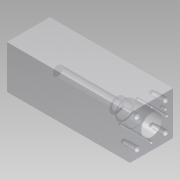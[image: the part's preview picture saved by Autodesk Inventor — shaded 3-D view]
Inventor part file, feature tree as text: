
AUTODESK INVENTOR PART (.ipt)
format: ipt  version: 2014 (Build 180170000, 170)  size: 363,008 bytes
history: native  units: mm
features: other x48, extrude x23, sketch x23
ambient origin geometry x8: Origin, YZ Plane, XZ Plane, XY Plane, X Axis, Y Axis, Z Axis, Center Point
bodies: 实体1 (feature_tree)
feature tree (94):
  extrude  "拉伸1"  Depth=33.7mm
  other  "UCS1"
  other  "UCS2"
  other  "UCS3"
  other  "UCS4"
  other  "UCS5"
  other  "UCS6"
  extrude  "拉伸23"  Depth=35.0mm
  extrude  "拉伸24"  Depth=65.0mm
  extrude  "拉伸25"  Depth=32.0mm
  extrude  "拉伸26"  Depth=43.0mm
  extrude  "拉伸28"  Depth=25.0mm
  extrude  "拉伸29"  Depth=16.0mm
  extrude  "拉伸30"  Depth=152.4mm
  extrude  "拉伸31"  Depth=23.0mm
  extrude  "拉伸32"  Depth=23.0mm
  extrude  "拉伸33"  Depth=23.0mm
  extrude  "拉伸34"  Depth=23.0mm
  extrude  "拉伸35"  Depth=24.0mm TaperAngle=0.0deg
  extrude  "拉伸36"  Depth=24.0mm
  extrude  "拉伸37"  Depth=24.0mm
  extrude  "拉伸39"  Depth=16.0mm TaperAngle=0.0deg
  extrude  "拉伸41"  TaperAngle=0.0deg  [1 undecoded]
  extrude  "拉伸42"  Depth=25.000195mm
  extrude  "拉伸43"  Depth=24.0mm TaperAngle=0.0deg
  extrude  "拉伸54"  Depth=27.0mm
  extrude  "拉伸55"  Depth=4.0mm
  extrude  "拉伸56"  Depth=25.0mm
  extrude  "拉伸57"  TaperAngle=0.0deg  [1 undecoded]
  sketch  "草图1"  dims[d0=70.0mm d1=0.0mm]
  sketch  "草图27"  dims[d2=0.0mm d3=0.0mm d4=0.0mm d5=0.0mm d6=0.0mm d7=0.0mm]
  sketch  "草图28"  dims[d8=0.0mm d9=0.0mm d10=0.0mm d11=0.0mm d12=0.0mm d13=0.0mm]
  sketch  "草图29"  dims[d14=0.0mm d15=0.0mm d16=0.0mm d17=0.0mm d18=0.0mm d19=0.0mm]
  sketch  "草图31"  dims[d20=0.0mm d21=0.0mm d22=0.0mm d23=0.0mm d24=0.0mm d25=0.0mm]
  sketch  "草图32"  dims[d26=0.0mm d27=0.0mm d28=0.0mm d29=0.0mm d30=0.0mm d31=0.0mm]
  sketch  "草图33"  dims[d32=0.0mm d33=0.0mm d34=0.0mm d35=0.0mm d36=0.0mm d37=0.0mm d110=33.7mm]
  sketch  "草图34"  dims[d111=36.0mm d112=35.0mm]
  sketch  "草图35"  dims[d113=65.0mm d114=65.0mm]
  sketch  "草图36"  dims[d115=10.0mm d116=-2.617994mm d117=32.0mm]
  sketch  "草图37"  dims[d118=43.0mm d119=0.0mm d120=26.07mm]
  sketch  "草图38"  dims[d121=13.0mm d122=-2.617994mm d124=25.0mm]
  sketch  "草图39"  dims[d125=56.0mm d126=0.0mm d127=16.0mm]
  sketch  "草图40"  dims[d130=152.4mm d131=0.0mm d132=152.4mm d133=-10.297443mm]
  sketch  "草图41"  dims[d134=6.75mm d135=23.0mm]
  sketch  "草图43"  dims[d136=23.0mm d137=23.0mm]
  sketch  "草图45"  dims[d138=23.0mm d139=23.0mm]
  sketch  "草图46"  dims[d140=23.0mm d141=23.0mm]
  sketch  "草图47"  dims[d142=23.0mm d143=24.0mm d144=0.0mm]
  sketch  "草图64"  dims[d145=24.0mm d146=-10.297443mm d147=24.0mm d148=-10.297443mm]
  sketch  "草图65"  dims[d149=24.0mm d150=-10.297443mm d151=24.0mm d152=-10.297443mm]
  sketch  "草图66"  dims[d153=8.0mm d154=16.0mm d155=0.0mm]
  sketch  "草图67"  dims[d156=4.0mm d160=0.0mm d163=25.000195mm d164=24.0mm d165=0.0mm d166=25.4mm d167=-10.297443mm d170=4.0mm d172=25.0mm d173=0.0mm d176=26.0mm d177=0.0mm d180=25.4mm d181=-10.297443mm d182=4.0mm d183=23.0mm d184=10.5mm d185=8.0mm d186=0.0mm d187=8.0mm d188=-10.297443mm d294=70.0mm d295=200.0mm d296=0.0mm d297=25.0mm d298=4.0mm d299=25.0mm d300=0.0mm d301=25.0mm d302=-10.297443mm d303=0.0mm d304=25.0mm d305=4.0mm d306=27.0mm d307=0.0mm d308=27.0mm d309=-10.297443mm]
  other  "UCS1: YZ 平面"
  other  "UCS1: XZ 平面"
  other  "UCS1: XY 平面"
  other  "UCS1: X 轴"
  other  "UCS1: Y 轴"
  other  "UCS1: Z 轴"
  other  "UCS1: 原点"
  other  "UCS2: YZ 平面"
  other  "UCS2: XZ 平面"
  other  "UCS2: XY 平面"
  other  "UCS2: X 轴"
  other  "UCS2: Y 轴"
  other  "UCS2: Z 轴"
  other  "UCS2: 原点"
  other  "UCS3: YZ 平面"
  other  "UCS3: XZ 平面"
  other  "UCS3: XY 平面"
  other  "UCS3: X 轴"
  other  "UCS3: Y 轴"
  other  "UCS3: Z 轴"
  other  "UCS3: 原点"
  other  "UCS4: YZ 平面"
  other  "UCS4: XZ 平面"
  other  "UCS4: XY 平面"
  other  "UCS4: X 轴"
  other  "UCS4: Y 轴"
  other  "UCS4: Z 轴"
  other  "UCS4: 原点"
  other  "UCS5: YZ 平面"
  other  "UCS5: XZ 平面"
  other  "UCS5: XY 平面"
  other  "UCS5: X 轴"
  other  "UCS5: Y 轴"
  other  "UCS5: Z 轴"
  other  "UCS5: 原点"
  other  "UCS6: YZ 平面"
  other  "UCS6: XZ 平面"
  other  "UCS6: XY 平面"
  other  "UCS6: X 轴"
  other  "UCS6: Y 轴"
  other  "UCS6: Z 轴"
  other  "UCS6: 原点"
note: 2 required parameter values undecoded (feature->parameter linkage not recoverable at this tier; creation-order binding heuristic only, values carry confidence <= 0.55)
